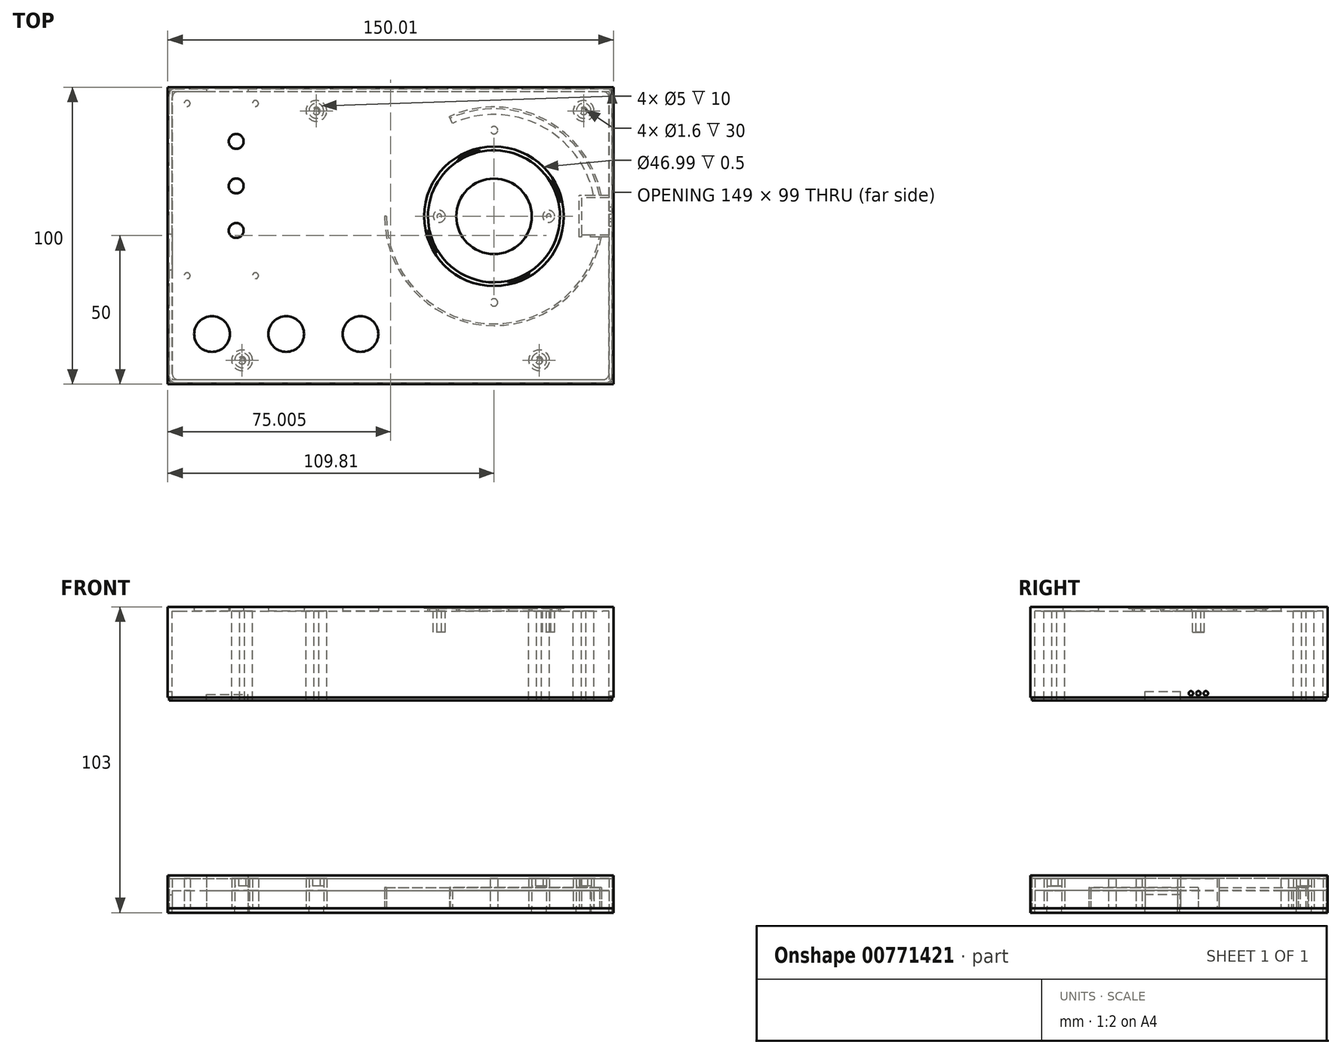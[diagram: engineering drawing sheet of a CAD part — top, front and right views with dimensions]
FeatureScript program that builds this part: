
annotation { "Feature Type Name" : "Feature", "Feature Type Description" : "" }
export const myFeature = defineFeature(function(context is Context, id is Id, definition is map)
    precondition{}
    {
        {
            var Q0;
            Q0=qCreatedBy(makeId("Top.planeOp"),FACE);
            var sketch = newSketch(context, id + "F0", { "sketchPlane" : qUnion([Q0])});
            skArc(sketch, "E0", {"start": v(-36.2, 0) * mm, "mid": v(-3.52, -36.02) * mm, "end": v(35.51, -7) * mm});
            skArc(sketch, "E1.0", {"start": v(-14.02, 31.3) * mm, "mid": v(15.6, 30.54) * mm, "end": v(33.57, 7) * mm});
            skCircle(sketch, "E2", {"center": v(0, 29) * mm, "radius": 2.5 * mm});
            skCircle(sketch, "E3", {"center": v(0, 29) * mm, "radius": 1.25 * mm});
            skCircle(sketch, "E4.1.0.0", {"center": v(0, -29) * mm, "radius": 2.5 * mm});
            skCircle(sketch, "E4.1.0.1", {"center": v(0, -29) * mm, "radius": 1.25 * mm});
            skLineSegment(sketch, "E4.direction1", {"start": v(0, 29) * mm, "end": v(0, -29) * mm, "construction": true});
            skArc(sketch, "E5", {"start": v(-36.83, 0) * mm, "mid": v(-3.52, -36.66) * mm, "end": v(36.16, -7) * mm});
            skPoint(sketch, "E6.middle", {"position": v(36.2, 0) * mm});
            skLineSegment(sketch, "E7.bottom", {"start": v(38.7, -7) * mm, "end": v(28.7, -7) * mm});
            skLineSegment(sketch, "E7.top", {"start": v(38.7, 7) * mm, "end": v(28.7, 7) * mm});
            skLineSegment(sketch, "E7.right", {"start": v(28.7, -7) * mm, "end": v(28.7, 7) * mm});
            skLineSegment(sketch, "E8", {"start": v(-34.3, 0) * mm, "end": v(-36.83, 0) * mm});
            skLineSegment(sketch, "E9", {"start": v(-14.02, 31.3) * mm, "end": v(-15.06, 33.61) * mm});
            skArc(sketch, "E10.trimOffspring", {"start": v(36.16, 7) * mm, "mid": v(16.98, 32.68) * mm, "end": v(-15.06, 33.61) * mm});
            skArc(sketch, "E11.trimOffspring", {"start": v(35.51, 7) * mm, "mid": v(16.63, 32.15) * mm, "end": v(-14.8, 33.03) * mm});
            skArc(sketch, "E12.trimOffspring", {"start": v(33.57, -7) * mm, "mid": v(-3.52, -34.1) * mm, "end": v(-34.3, 0) * mm});
            skCircle(sketch, "E13", {"center": v(-103.3, 38) * mm, "radius": 1 * mm});
            skCircle(sketch, "E14", {"center": v(-103.3, 38) * mm, "radius": 3 * mm});
            skCircle(sketch, "E15.1.0.0", {"center": v(-80.3, 38) * mm, "radius": 3 * mm});
            skCircle(sketch, "E15.1.0.1", {"center": v(-80.3, 38) * mm, "radius": 1 * mm});
            skLineSegment(sketch, "E15.direction1", {"start": v(-103.3, 38) * mm, "end": v(-80.3, 38) * mm, "construction": true});
            skLineSegment(sketch, "E16.1.0.0", {"start": v(-103.3, -20) * mm, "end": v(-80.3, -20) * mm, "construction": true});
            skCircle(sketch, "E16.1.0.1", {"center": v(-103.3, -20) * mm, "radius": 1 * mm});
            skCircle(sketch, "E16.1.0.2", {"center": v(-80.3, -20) * mm, "radius": 3 * mm});
            skCircle(sketch, "E16.1.0.3", {"center": v(-80.3, -20) * mm, "radius": 1 * mm});
            skCircle(sketch, "E16.1.0.4", {"center": v(-103.3, -20) * mm, "radius": 3 * mm});
            skLineSegment(sketch, "E16.direction1", {"start": v(-103.3, 38) * mm, "end": v(-103.3, -20) * mm, "construction": true});
            skLineSegment(sketch, "E17.bottom", {"start": v(-108.3, 42) * mm, "end": v(38.7, 42) * mm});
            skLineSegment(sketch, "E17.top", {"start": v(-108.3, -55) * mm, "end": v(38.7, -55) * mm});
            skLineSegment(sketch, "E17.left", {"start": v(-108.3, 42) * mm, "end": v(-108.3, -55) * mm});
            skLineSegment(sketch, "E17.right", {"start": v(38.7, 42) * mm, "end": v(38.7, -55) * mm});
            skLineSegment(sketch, "E18.0", {"start": v(-109.8, 43.5) * mm, "end": v(40.2, 43.5) * mm});
            skLineSegment(sketch, "E18.1", {"start": v(-109.8, 43.5) * mm, "end": v(-109.8, -56.5) * mm});
            skLineSegment(sketch, "E18.2", {"start": v(-109.8, -56.5) * mm, "end": v(40.2, -56.5) * mm});
            skLineSegment(sketch, "E18.3", {"start": v(40.2, 43.5) * mm, "end": v(40.2, -56.5) * mm});
            skLineSegment(sketch, "E19.0", {"start": v(38.7, -6.3) * mm, "end": v(29.4, -6.3) * mm});
            skLineSegment(sketch, "E19.1", {"start": v(29.4, -6.3) * mm, "end": v(29.4, 6.3) * mm});
            skLineSegment(sketch, "E19.2", {"start": v(38.7, 6.3) * mm, "end": v(29.4, 6.3) * mm});
            skLineSegment(sketch, "E20", {"start": v(38.7, 7) * mm, "end": v(38.7, 6.3) * mm});
            skLineSegment(sketch, "E21", {"start": v(38.7, -6.3) * mm, "end": v(38.7, -7) * mm});
            skLineSegment(sketch, "E22", {"start": v(29.4, -6.3) * mm, "end": v(29.4, -7) * mm});
            skLineSegment(sketch, "E23", {"start": v(32.4, -6.3) * mm, "end": v(32.4, -7) * mm});
            skLineSegment(sketch, "E24", {"start": v(-109.8, -18) * mm, "end": v(-108.3, -18) * mm});
            skLineSegment(sketch, "E25", {"start": v(-109.8, -6) * mm, "end": v(-108.3, -6) * mm});
            skLineSegment(sketch, "E26", {"start": v(-96.8, 43.5) * mm, "end": v(-96.8, 42) * mm});
            skLineSegment(sketch, "E27", {"start": v(-82.8, 43.5) * mm, "end": v(-82.8, 42) * mm});
            skCircle(sketch, "E28", {"center": v(-84.8, -48.5) * mm, "radius": 3.5 * mm});
            skCircle(sketch, "E29", {"center": v(-84.8, -48.5) * mm, "radius": 2.5 * mm});
            skCircle(sketch, "E30", {"center": v(-84.8, -48.5) * mm, "radius": 1.25 * mm});
            skCircle(sketch, "E31", {"center": v(15.2, -48.5) * mm, "radius": 3.5 * mm});
            skCircle(sketch, "E32", {"center": v(15.2, -48.5) * mm, "radius": 2.5 * mm});
            skCircle(sketch, "E33", {"center": v(15.2, -48.5) * mm, "radius": 1.25 * mm});
            skCircle(sketch, "E34", {"center": v(-59.8, 35.5) * mm, "radius": 3.5 * mm});
            skCircle(sketch, "E35", {"center": v(-59.8, 35.5) * mm, "radius": 2.5 * mm});
            skCircle(sketch, "E36", {"center": v(-59.8, 35.5) * mm, "radius": 1.25 * mm});
            skCircle(sketch, "E37", {"center": v(30.2, 35.5) * mm, "radius": 3.5 * mm});
            skCircle(sketch, "E38", {"center": v(30.2, 35.5) * mm, "radius": 2.5 * mm});
            skCircle(sketch, "E39", {"center": v(30.2, 35.5) * mm, "radius": 1.25 * mm});
            skLineSegment(sketch, "E40.0", {"start": v(-109.3, -56) * mm, "end": v(39.7, -56) * mm});
            skLineSegment(sketch, "E40.1", {"start": v(-109.3, 43) * mm, "end": v(-109.3, -6) * mm});
            skLineSegment(sketch, "E40.2", {"start": v(-109.3, 43) * mm, "end": v(-96.8, 43) * mm});
            skLineSegment(sketch, "E40.3", {"start": v(39.7, 43) * mm, "end": v(39.7, -56) * mm});
            skLineSegment(sketch, "E41.trimOffspring", {"start": v(-109.3, -18) * mm, "end": v(-109.3, -56) * mm});
            skLineSegment(sketch, "E42.trimOffspring", {"start": v(-82.8, 43) * mm, "end": v(39.7, 43) * mm});
            skSolve(sketch);
        }
        {
            var Q0;
            {var subQ0=sQuery(id+"F0.wireOp",EDGE,"E1.0");Q0=makeQuery(id+"F0.imprint","IMPRINT",FACE,{"disambiguationData":[TD([[makeQuery(id+"F0.imprint","IMPRINT",EDGE,{"derivedFrom":subQ0}),1.0]])]});}
            var Q1;
            {var subQ0=sQuery(id+"F0.wireOp",EDGE,"E0");Q1=makeQuery(id+"F0.imprint","IMPRINT",FACE,{"disambiguationData":[TD([[makeQuery(id+"F0.imprint","IMPRINT",EDGE,{"derivedFrom":subQ0}),1.0]])]});}
            var Q2;
            Q2=makeQuery(id+"F0.imprint","IMPRINT",FACE,{"disambiguationData":[TD([[makeQuery(id+"F0.imprint","IMPRINT",EDGE,{"derivedFrom":sQuery(id+"F0.wireOp",EDGE,"E4.1.0.0")}),1.0]])]});
            var Q3;
            Q3=makeQuery(id+"F0.imprint","IMPRINT",FACE,{"disambiguationData":[TD([[makeQuery(id+"F0.imprint","IMPRINT",EDGE,{"derivedFrom":sQuery(id+"F0.wireOp",EDGE,"E2")}),1.0]])]});
            var Q4;
            Q4=makeQuery(id+"F0.imprint","IMPRINT",FACE,{"disambiguationData":[TD([[makeQuery(id+"F0.imprint","IMPRINT",EDGE,{"derivedFrom":sQuery(id+"F0.wireOp",EDGE,"E15.1.0.0")}),1.0]])]});
            var Q5;
            Q5=makeQuery(id+"F0.imprint","IMPRINT",FACE,{"disambiguationData":[TD([[makeQuery(id+"F0.imprint","IMPRINT",EDGE,{"derivedFrom":sQuery(id+"F0.wireOp",EDGE,"E13")}),-1.0]])]});
            var Q6;
            Q6=makeQuery(id+"F0.imprint","IMPRINT",FACE,{"disambiguationData":[TD([[makeQuery(id+"F0.imprint","IMPRINT",EDGE,{"derivedFrom":sQuery(id+"F0.wireOp",EDGE,"E16.1.0.2")}),1.0]])]});
            var Q7;
            Q7=makeQuery(id+"F0.imprint","IMPRINT",FACE,{"disambiguationData":[TD([[makeQuery(id+"F0.imprint","IMPRINT",EDGE,{"derivedFrom":sQuery(id+"F0.wireOp",EDGE,"E16.1.0.1")}),-1.0]])]});
            var Q8;
            {var subQ0=sQuery(id+"F0.wireOp",EDGE,"E22");Q8=makeQuery(id+"F0.imprint","IMPRINT",FACE,{"disambiguationData":[TD([[makeQuery(id+"F0.imprint","IMPRINT",EDGE,{"derivedFrom":subQ0}),1.0]])]});}
            var Q9;
            {var subQ0=sQuery(id+"F0.wireOp",EDGE,"E26");Q9=makeQuery(id+"F0.imprint","IMPRINT",FACE,{"disambiguationData":[TD([[makeQuery(id+"F0.imprint","IMPRINT",EDGE,{"derivedFrom":subQ0}),1.0]])]});}
            extrude(context, id + "F1", {"entities" : qUnion([Q0, Q1, Q2, Q3, Q4, Q5, Q6, Q7, Q8, Q9]), "depth" : 6 * mm, "offsetDistance" : 25 * mm});
        }
        {
            var Q0;
            Q0=makeQuery(id+"F0.imprint","IMPRINT",FACE,{"disambiguationData":[TD([[makeQuery(id+"F0.imprint","IMPRINT",EDGE,{"derivedFrom":sQuery(id+"F0.wireOp",EDGE,"E3")}),1.0]])]});
            var Q1;
            Q1=makeQuery(id+"F0.imprint","IMPRINT",FACE,{"disambiguationData":[TD([[makeQuery(id+"F0.imprint","IMPRINT",EDGE,{"derivedFrom":sQuery(id+"F0.wireOp",EDGE,"E4.1.0.1")}),1.0]])]});
            var Q2;
            Q2=makeQuery(id+"F0.imprint","IMPRINT",FACE,{"disambiguationData":[TD([[makeQuery(id+"F0.imprint","IMPRINT",EDGE,{"derivedFrom":sQuery(id+"F0.wireOp",EDGE,"E13")}),1.0]])]});
            var Q3;
            Q3=makeQuery(id+"F0.imprint","IMPRINT",FACE,{"disambiguationData":[TD([[makeQuery(id+"F0.imprint","IMPRINT",EDGE,{"derivedFrom":sQuery(id+"F0.wireOp",EDGE,"E15.1.0.1")}),1.0]])]});
            var Q4;
            Q4=makeQuery(id+"F0.imprint","IMPRINT",FACE,{"disambiguationData":[TD([[makeQuery(id+"F0.imprint","IMPRINT",EDGE,{"derivedFrom":sQuery(id+"F0.wireOp",EDGE,"E16.1.0.3")}),1.0]])]});
            var Q5;
            Q5=makeQuery(id+"F0.imprint","IMPRINT",FACE,{"disambiguationData":[TD([[makeQuery(id+"F0.imprint","IMPRINT",EDGE,{"derivedFrom":sQuery(id+"F0.wireOp",EDGE,"E16.1.0.1")}),1.0]])]});
            extrude(context, id + "F2", {"entities" : qUnion([Q0, Q1, Q2, Q3, Q4, Q5]), "depth" : 10 * mm, "offsetDistance" : 25 * mm});
        }
        {
            var Q0;
            {var subQ0=sQuery(id+"F0.wireOp",EDGE,"E7.right");Q0=makeQuery(id+"F0.imprint","IMPRINT",FACE,{"disambiguationData":[TD([[makeQuery(id+"F0.imprint","IMPRINT",EDGE,{"derivedFrom":subQ0}),-1.0]])]});}
            var Q1;
            {var subQ4=sQuery(id+"F0.wireOp",EDGE,"E21");Q1=makeQuery(id+"F0.imprint","IMPRINT",FACE,{"disambiguationData":[TD([[makeQuery(id+"F0.imprint","IMPRINT",EDGE,{"derivedFrom":subQ4}),-1.0]])]});}
            var Q2;
            Q2=makeQuery(id+"F0.imprint","IMPRINT",FACE,{"disambiguationData":[TD([[makeQuery(id+"F0.imprint","IMPRINT",EDGE,{"derivedFrom":sQuery(id+"F0.wireOp",EDGE,"E31")}),1.0]])]});
            var Q3;
            Q3=makeQuery(id+"F0.imprint","IMPRINT",FACE,{"disambiguationData":[TD([[makeQuery(id+"F0.imprint","IMPRINT",EDGE,{"derivedFrom":sQuery(id+"F0.wireOp",EDGE,"E37")}),1.0]])]});
            var Q4;
            Q4=makeQuery(id+"F0.imprint","IMPRINT",FACE,{"disambiguationData":[TD([[makeQuery(id+"F0.imprint","IMPRINT",EDGE,{"derivedFrom":sQuery(id+"F0.wireOp",EDGE,"E28")}),1.0]])]});
            var Q5;
            Q5=makeQuery(id+"F0.imprint","IMPRINT",FACE,{"disambiguationData":[TD([[makeQuery(id+"F0.imprint","IMPRINT",EDGE,{"derivedFrom":sQuery(id+"F0.wireOp",EDGE,"E34")}),1.0]])]});
            extrude(context, id + "F3", {"entities" : qUnion([Q0, Q1, Q2, Q3, Q4, Q5]), "depth" : 10 * mm, "offsetDistance" : 25 * mm});
        }
        {
            var Q0;
            {var subQ3=sQuery(id+"F0.wireOp",EDGE,"8f94c075-a68a-4a81-960c-e8ac357c0ef5.0");Q0=makeQuery(id+"F0.imprint","IMPRINT",FACE,{"disambiguationData":[TD([[makeQuery(id+"F0.imprint","IMPRINT",EDGE,{"derivedFrom":subQ3}),-1.0]])]});}
            var Q1;
            {var subQ11=sQuery(id+"F0.wireOp",EDGE,"E17.top");Q1=makeQuery(id+"F0.imprint","IMPRINT",FACE,{"disambiguationData":[TD([[makeQuery(id+"F0.imprint","IMPRINT",EDGE,{"derivedFrom":subQ11}),-1.0]])]});}
            var Q2;
            {var subQ3=sQuery(id+"F0.wireOp",EDGE,"E40.1");Q2=makeQuery(id+"F0.imprint","IMPRINT",FACE,{"disambiguationData":[TD([[makeQuery(id+"F0.imprint","IMPRINT",EDGE,{"derivedFrom":subQ3}),1.0]])]});}
            extrude(context, id + "F4", {"entities" : qUnion([Q0, Q1, Q2]), "depth" : 10 * mm, "offsetDistance" : 25 * mm});
        }
        {
            var Q0;
            {var subQ0=sQuery(id+"F0.wireOp",EDGE,"E24");Q0=makeQuery(id+"F0.imprint","IMPRINT",FACE,{"disambiguationData":[TD([[makeQuery(id+"F0.imprint","IMPRINT",EDGE,{"derivedFrom":subQ0}),1.0]])]});}
            extrude(context, id + "F5", {"entities" : qUnion([Q0]), "depth" : 4.5 * mm, "offsetDistance" : 25 * mm});
        }
        {
            var Q0;
            {var subQ8=sQuery(id+"F0.wireOp",EDGE,"8f94c075-a68a-4a81-960c-e8ac357c0ef5.0");Q0=makeQuery(id+"F0.imprint","IMPRINT",FACE,{"disambiguationData":[TD([[makeQuery(id+"F0.imprint","IMPRINT",EDGE,{"derivedFrom":subQ8}),1.0]])]});}
            var Q1;
            {var subQ0=sQuery(id+"F0.wireOp",EDGE,"E18.2");Q1=makeQuery(id+"F0.imprint","IMPRINT",FACE,{"disambiguationData":[TD([[makeQuery(id+"F0.imprint","IMPRINT",EDGE,{"derivedFrom":subQ0}),1.0]])]});}
            var Q2;
            {var subQ3=sQuery(id+"F0.wireOp",EDGE,"E40.1");Q2=makeQuery(id+"F0.imprint","IMPRINT",FACE,{"disambiguationData":[TD([[makeQuery(id+"F0.imprint","IMPRINT",EDGE,{"derivedFrom":subQ3}),-1.0]])]});}
            extrude(context, id + "F6", {"entities" : qUnion([Q0, Q1, Q2]), "depth" : 11 * mm, "offsetDistance" : 25 * mm});
        }
        {
            var Q0;
            {var subQ0=sQuery(id+"F0.wireOp",EDGE,"E10.trimOffspring");Q0=makeQuery(id+"F0.imprint","IMPRINT",FACE,{"disambiguationData":[TD([[makeQuery(id+"F0.imprint","IMPRINT",EDGE,{"derivedFrom":subQ0}),1.0]])]});}
            var Q1;
            {var subQ0=sQuery(id+"F0.wireOp",EDGE,"E0");Q1=makeQuery(id+"F0.imprint","IMPRINT",FACE,{"disambiguationData":[TD([[makeQuery(id+"F0.imprint","IMPRINT",EDGE,{"derivedFrom":subQ0}),-1.0]])]});}
            extrude(context, id + "F7", {"entities" : qUnion([Q0, Q1]), "depth" : 7 * mm, "offsetDistance" : 25 * mm});
        }
        {
            var Q0;
            Q0=makeQuery(id+"F0.imprint","IMPRINT",FACE,{"disambiguationData":[TD([[makeQuery(id+"F0.imprint","IMPRINT",EDGE,{"derivedFrom":sQuery(id+"F0.wireOp",EDGE,"E29")}),1.0]])]});
            var Q1;
            Q1=makeQuery(id+"F0.imprint","IMPRINT",FACE,{"disambiguationData":[TD([[makeQuery(id+"F0.imprint","IMPRINT",EDGE,{"derivedFrom":sQuery(id+"F0.wireOp",EDGE,"E35")}),1.0]])]});
            var Q2;
            Q2=makeQuery(id+"F0.imprint","IMPRINT",FACE,{"disambiguationData":[TD([[makeQuery(id+"F0.imprint","IMPRINT",EDGE,{"derivedFrom":sQuery(id+"F0.wireOp",EDGE,"E32")}),1.0]])]});
            var Q3;
            Q3=makeQuery(id+"F0.imprint","IMPRINT",FACE,{"disambiguationData":[TD([[makeQuery(id+"F0.imprint","IMPRINT",EDGE,{"derivedFrom":sQuery(id+"F0.wireOp",EDGE,"E38")}),1.0]])]});
            extrude(context, id + "F8", {"entities" : qUnion([Q0, Q1, Q2, Q3]), "depth" : 10 * mm, "offsetDistance" : 25 * mm, "hasSecondDirection" : true, "secondDirectionOppositeDirection" : true, "secondDirectionDepth" : -7.5 * mm});
        }
        {
            var Q0;
            {var subQ0=sQuery(id+"F0.wireOp",EDGE,"E18.2");Q0=makeQuery(id+"F0.imprint","IMPRINT",FACE,{"disambiguationData":[TD([[makeQuery(id+"F0.imprint","IMPRINT",EDGE,{"derivedFrom":subQ0}),1.0]])]});}
            var Q1;
            {var subQ2=sQuery(id+"F0.wireOp",EDGE,"E20");Q1=makeQuery(id+"F0.imprint","IMPRINT",FACE,{"disambiguationData":[TD([[makeQuery(id+"F0.imprint","IMPRINT",EDGE,{"derivedFrom":subQ2}),1.0]])]});}
            var Q2;
            {var subQ0=sQuery(id+"F0.wireOp",EDGE,"E24");var subQ1=sQuery(id+"F0.wireOp",EDGE,"E17.left");var subQ2=makeQuery(id+"F0.imprint","INTERSECT",VERTEX,{"derivedFrom":[subQ1,subQ0]});Q2=makeQuery(id+"F0.imprint","IMPRINT",FACE,{"disambiguationData":[TD([[makeQuery(id+"F0.imprint","IMPRINT",EDGE,{"disambiguationData":[TD([[subQ2,1.0]])],"derivedFrom":subQ1}),-1.0]])]});}
            var Q3;
            {var subQ3=sQuery(id+"F0.wireOp",EDGE,"E40.1");Q3=makeQuery(id+"F0.imprint","IMPRINT",FACE,{"disambiguationData":[TD([[makeQuery(id+"F0.imprint","IMPRINT",EDGE,{"derivedFrom":subQ3}),-1.0]])]});}
            var Q4;
            {var subQ3=sQuery(id+"F0.wireOp",EDGE,"E40.1");Q4=makeQuery(id+"F0.imprint","IMPRINT",FACE,{"disambiguationData":[TD([[makeQuery(id+"F0.imprint","IMPRINT",EDGE,{"derivedFrom":subQ3}),1.0]])]});}
            var Q5;
            {var subQ0=sQuery(id+"F0.wireOp",EDGE,"E26");var subQ4=sQuery(id+"F0.wireOp",EDGE,"E17.bottom");var subQ5=makeQuery(id+"F0.imprint","INTERSECT",VERTEX,{"derivedFrom":[subQ4,subQ0]});Q5=makeQuery(id+"F0.imprint","IMPRINT",FACE,{"disambiguationData":[TD([[makeQuery(id+"F0.imprint","IMPRINT",EDGE,{"disambiguationData":[TD([[subQ5,-1.0]])],"derivedFrom":subQ4}),1.0]])]});}
            var Q6;
            {var subQ8=sQuery(id+"F0.wireOp",EDGE,"E1.0");Q6=makeQuery(id+"F0.imprint","IMPRINT",FACE,{"disambiguationData":[TD([[makeQuery(id+"F0.imprint","IMPRINT",EDGE,{"derivedFrom":subQ8}),-1.0]])]});}
            var Q7;
            Q7=makeQuery(id+"F0.imprint","IMPRINT",FACE,{"disambiguationData":[TD([[makeQuery(id+"F0.imprint","IMPRINT",EDGE,{"derivedFrom":sQuery(id+"F0.wireOp",EDGE,"E13")}),-1.0]])]});
            var Q8;
            Q8=makeQuery(id+"F0.imprint","IMPRINT",FACE,{"disambiguationData":[TD([[makeQuery(id+"F0.imprint","IMPRINT",EDGE,{"derivedFrom":sQuery(id+"F0.wireOp",EDGE,"E13")}),1.0]])]});
            var Q9;
            Q9=makeQuery(id+"F0.imprint","IMPRINT",FACE,{"disambiguationData":[TD([[makeQuery(id+"F0.imprint","IMPRINT",EDGE,{"derivedFrom":sQuery(id+"F0.wireOp",EDGE,"E15.1.0.0")}),1.0]])]});
            var Q10;
            Q10=makeQuery(id+"F0.imprint","IMPRINT",FACE,{"disambiguationData":[TD([[makeQuery(id+"F0.imprint","IMPRINT",EDGE,{"derivedFrom":sQuery(id+"F0.wireOp",EDGE,"E15.1.0.1")}),1.0]])]});
            var Q11;
            Q11=makeQuery(id+"F0.imprint","IMPRINT",FACE,{"disambiguationData":[TD([[makeQuery(id+"F0.imprint","IMPRINT",EDGE,{"derivedFrom":sQuery(id+"F0.wireOp",EDGE,"E34")}),1.0]])]});
            var Q12;
            Q12=makeQuery(id+"F0.imprint","IMPRINT",FACE,{"disambiguationData":[TD([[makeQuery(id+"F0.imprint","IMPRINT",EDGE,{"derivedFrom":sQuery(id+"F0.wireOp",EDGE,"E28")}),1.0]])]});
            var Q13;
            Q13=makeQuery(id+"F0.imprint","IMPRINT",FACE,{"disambiguationData":[TD([[makeQuery(id+"F0.imprint","IMPRINT",EDGE,{"derivedFrom":sQuery(id+"F0.wireOp",EDGE,"E16.1.0.1")}),-1.0]])]});
            var Q14;
            Q14=makeQuery(id+"F0.imprint","IMPRINT",FACE,{"disambiguationData":[TD([[makeQuery(id+"F0.imprint","IMPRINT",EDGE,{"derivedFrom":sQuery(id+"F0.wireOp",EDGE,"E16.1.0.1")}),1.0]])]});
            var Q15;
            Q15=makeQuery(id+"F0.imprint","IMPRINT",FACE,{"disambiguationData":[TD([[makeQuery(id+"F0.imprint","IMPRINT",EDGE,{"derivedFrom":sQuery(id+"F0.wireOp",EDGE,"E16.1.0.2")}),1.0]])]});
            var Q16;
            Q16=makeQuery(id+"F0.imprint","IMPRINT",FACE,{"disambiguationData":[TD([[makeQuery(id+"F0.imprint","IMPRINT",EDGE,{"derivedFrom":sQuery(id+"F0.wireOp",EDGE,"E16.1.0.3")}),1.0]])]});
            var Q17;
            Q17=makeQuery(id+"F0.imprint","IMPRINT",FACE,{"disambiguationData":[TD([[makeQuery(id+"F0.imprint","IMPRINT",EDGE,{"derivedFrom":sQuery(id+"F0.wireOp",EDGE,"E2")}),1.0]])]});
            var Q18;
            Q18=makeQuery(id+"F0.imprint","IMPRINT",FACE,{"disambiguationData":[TD([[makeQuery(id+"F0.imprint","IMPRINT",EDGE,{"derivedFrom":sQuery(id+"F0.wireOp",EDGE,"E3")}),1.0]])]});
            var Q19;
            {var subQ0=sQuery(id+"F0.wireOp",EDGE,"E1.0");Q19=makeQuery(id+"F0.imprint","IMPRINT",FACE,{"disambiguationData":[TD([[makeQuery(id+"F0.imprint","IMPRINT",EDGE,{"derivedFrom":subQ0}),1.0]])]});}
            var Q20;
            {var subQ0=sQuery(id+"F0.wireOp",EDGE,"E10.trimOffspring");Q20=makeQuery(id+"F0.imprint","IMPRINT",FACE,{"disambiguationData":[TD([[makeQuery(id+"F0.imprint","IMPRINT",EDGE,{"derivedFrom":subQ0}),1.0]])]});}
            var Q21;
            {var subQ1=sQuery(id+"F0.wireOp",EDGE,"E0");Q21=makeQuery(id+"F0.imprint","IMPRINT",FACE,{"disambiguationData":[TD([[makeQuery(id+"F0.imprint","IMPRINT",EDGE,{"derivedFrom":subQ1}),1.0]])]});}
            var Q22;
            {var subQ0=sQuery(id+"F0.wireOp",EDGE,"E0");Q22=makeQuery(id+"F0.imprint","IMPRINT",FACE,{"disambiguationData":[TD([[makeQuery(id+"F0.imprint","IMPRINT",EDGE,{"derivedFrom":subQ0}),-1.0]])]});}
            var Q23;
            Q23=makeQuery(id+"F0.imprint","IMPRINT",FACE,{"disambiguationData":[TD([[makeQuery(id+"F0.imprint","IMPRINT",EDGE,{"derivedFrom":sQuery(id+"F0.wireOp",EDGE,"E37")}),1.0]])]});
            var Q24;
            {var subQ5=sQuery(id+"F0.wireOp",EDGE,"E7.right");Q24=makeQuery(id+"F0.imprint","IMPRINT",FACE,{"disambiguationData":[TD([[makeQuery(id+"F0.imprint","IMPRINT",EDGE,{"derivedFrom":subQ5}),-1.0]])]});}
            var Q25;
            {var subQ0=sQuery(id+"F0.wireOp",EDGE,"E19.1");Q25=makeQuery(id+"F0.imprint","IMPRINT",FACE,{"disambiguationData":[TD([[makeQuery(id+"F0.imprint","IMPRINT",EDGE,{"derivedFrom":subQ0}),-1.0]])]});}
            var Q26;
            {var subQ0=sQuery(id+"F0.wireOp",EDGE,"E21");Q26=makeQuery(id+"F0.imprint","IMPRINT",FACE,{"disambiguationData":[TD([[makeQuery(id+"F0.imprint","IMPRINT",EDGE,{"derivedFrom":subQ0}),-1.0]])]});}
            var Q27;
            {var subQ0=sQuery(id+"F0.wireOp",EDGE,"E22");Q27=makeQuery(id+"F0.imprint","IMPRINT",FACE,{"disambiguationData":[TD([[makeQuery(id+"F0.imprint","IMPRINT",EDGE,{"derivedFrom":subQ0}),1.0]])]});}
            var Q28;
            Q28=makeQuery(id+"F0.imprint","IMPRINT",FACE,{"disambiguationData":[TD([[makeQuery(id+"F0.imprint","IMPRINT",EDGE,{"derivedFrom":sQuery(id+"F0.wireOp",EDGE,"E4.1.0.0")}),1.0]])]});
            var Q29;
            Q29=makeQuery(id+"F0.imprint","IMPRINT",FACE,{"disambiguationData":[TD([[makeQuery(id+"F0.imprint","IMPRINT",EDGE,{"derivedFrom":sQuery(id+"F0.wireOp",EDGE,"E4.1.0.1")}),1.0]])]});
            var Q30;
            Q30=makeQuery(id+"F0.imprint","IMPRINT",FACE,{"disambiguationData":[TD([[makeQuery(id+"F0.imprint","IMPRINT",EDGE,{"derivedFrom":sQuery(id+"F0.wireOp",EDGE,"E31")}),1.0]])]});
            extrude(context, id + "F9", {"entities" : qUnion([Q0, Q1, Q2, Q3, Q4, Q5, Q6, Q7, Q8, Q9, Q10, Q11, Q12, Q13, Q14, Q15, Q16, Q17, Q18, Q19, Q20, Q21, Q22, Q23, Q24, Q25, Q26, Q27, Q28, Q29, Q30]), "oppositeDirection" : true, "depth" : 1.5 * mm, "offsetDistance" : 25 * mm});
        }
        {
            var Q0;
            Q0=makeQuery(id+"F4.opExtrude","SWEPT_EDGE",EDGE,{"disambiguationData":[OSD([sQuery(id+"F0.wireOp",EDGE,"E17.bottom"),sQuery(id+"F0.wireOp",EDGE,"E17.right")])]});
            var Q1;
            Q1=makeQuery(id+"F6.opExtrude","SWEPT_EDGE",EDGE,{"disambiguationData":[OSD([sQuery(id+"F0.wireOp",EDGE,"E40.3"),sQuery(id+"F0.wireOp",EDGE,"E42.trimOffspring")])]});
            var Q2;
            Q2=makeQuery(id+"F9.opExtrude","SWEPT_EDGE",EDGE,{"disambiguationData":[OSD([sQuery(id+"F0.wireOp",EDGE,"E18.0"),sQuery(id+"F0.wireOp",EDGE,"E18.3")])]});
            var Q3;
            Q3=makeQuery(id+"F6.opExtrude","SWEPT_EDGE",EDGE,{"disambiguationData":[OSD([sQuery(id+"F0.wireOp",EDGE,"E18.0"),sQuery(id+"F0.wireOp",EDGE,"E18.3")])]});
            var Q4;
            Q4=makeQuery(id+"F9.opExtrude","SWEPT_EDGE",EDGE,{"disambiguationData":[OSD([sQuery(id+"F0.wireOp",EDGE,"E18.2"),sQuery(id+"F0.wireOp",EDGE,"E18.3")])]});
            var Q5;
            Q5=makeQuery(id+"F6.opExtrude","SWEPT_EDGE",EDGE,{"disambiguationData":[OSD([sQuery(id+"F0.wireOp",EDGE,"E18.2"),sQuery(id+"F0.wireOp",EDGE,"E18.3")])]});
            var Q6;
            Q6=makeQuery(id+"F4.opExtrude","SWEPT_EDGE",EDGE,{"disambiguationData":[OSD([sQuery(id+"F0.wireOp",EDGE,"E17.top"),sQuery(id+"F0.wireOp",EDGE,"E17.right")])]});
            var Q7;
            Q7=makeQuery(id+"F6.opExtrude","SWEPT_EDGE",EDGE,{"disambiguationData":[OSD([sQuery(id+"F0.wireOp",EDGE,"E40.0"),sQuery(id+"F0.wireOp",EDGE,"E40.3")])]});
            var Q8;
            Q8=makeQuery(id+"F4.opExtrude","SWEPT_EDGE",EDGE,{"disambiguationData":[OSD([sQuery(id+"F0.wireOp",EDGE,"E17.bottom"),sQuery(id+"F0.wireOp",EDGE,"E17.left")])]});
            var Q9;
            Q9=makeQuery(id+"F6.opExtrude","SWEPT_EDGE",EDGE,{"disambiguationData":[OSD([sQuery(id+"F0.wireOp",EDGE,"E40.1"),sQuery(id+"F0.wireOp",EDGE,"E40.2")])]});
            var Q10;
            Q10=makeQuery(id+"F4.opExtrude","SWEPT_EDGE",EDGE,{"disambiguationData":[OSD([sQuery(id+"F0.wireOp",EDGE,"E17.top"),sQuery(id+"F0.wireOp",EDGE,"E17.left")])]});
            var Q11;
            Q11=makeQuery(id+"F6.opExtrude","SWEPT_EDGE",EDGE,{"disambiguationData":[OSD([sQuery(id+"F0.wireOp",EDGE,"E40.0"),sQuery(id+"F0.wireOp",EDGE,"E41.trimOffspring")])]});
            var Q12;
            Q12=makeQuery(id+"F9.opExtrude","SWEPT_EDGE",EDGE,{"disambiguationData":[OSD([sQuery(id+"F0.wireOp",EDGE,"E18.0"),sQuery(id+"F0.wireOp",EDGE,"E18.1")])]});
            var Q13;
            Q13=makeQuery(id+"F6.opExtrude","SWEPT_EDGE",EDGE,{"disambiguationData":[OSD([sQuery(id+"F0.wireOp",EDGE,"E18.0"),sQuery(id+"F0.wireOp",EDGE,"E18.1")])]});
            var Q14;
            Q14=makeQuery(id+"F9.opExtrude","SWEPT_EDGE",EDGE,{"disambiguationData":[OSD([sQuery(id+"F0.wireOp",EDGE,"E18.1"),sQuery(id+"F0.wireOp",EDGE,"E18.2")])]});
            var Q15;
            Q15=makeQuery(id+"F6.opExtrude","SWEPT_EDGE",EDGE,{"disambiguationData":[OSD([sQuery(id+"F0.wireOp",EDGE,"E18.1"),sQuery(id+"F0.wireOp",EDGE,"E18.2")])]});
            fillet(context, id + "F10", {"entities" : qUnion([Q0, Q1, Q2, Q3, Q4, Q5, Q6, Q7, Q8, Q9, Q10, Q11, Q12, Q13, Q14, Q15]), "radius" : 2 * mm, "tangentPropagation" : true, "allowEdgeOverflow" : false});
        }
        {
            var Q0;
            Q0=makeQuery(id+"F4.opExtrude","SWEPT_EDGE",EDGE,{"disambiguationData":[OSD([sQuery(id+"F0.wireOp",EDGE,"E40.0"),sQuery(id+"F0.wireOp",EDGE,"E40.3")])]});
            var Q1;
            Q1=makeQuery(id+"F4.opExtrude","SWEPT_EDGE",EDGE,{"disambiguationData":[OSD([sQuery(id+"F0.wireOp",EDGE,"E40.3"),sQuery(id+"F0.wireOp",EDGE,"E42.trimOffspring")])]});
            var Q2;
            Q2=makeQuery(id+"F4.opExtrude","SWEPT_EDGE",EDGE,{"disambiguationData":[OSD([sQuery(id+"F0.wireOp",EDGE,"E40.1"),sQuery(id+"F0.wireOp",EDGE,"E40.2")])]});
            var Q3;
            Q3=makeQuery(id+"F4.opExtrude","SWEPT_EDGE",EDGE,{"disambiguationData":[OSD([sQuery(id+"F0.wireOp",EDGE,"E40.0"),sQuery(id+"F0.wireOp",EDGE,"E41.trimOffspring")])]});
            fillet(context, id + "F11", {"entities" : qUnion([Q0, Q1, Q2, Q3]), "radius" : 2 * mm, "tangentPropagation" : true, "allowEdgeOverflow" : false});
        }
        {
            var Q0;
            Q0=qCreatedBy(makeId("Top.planeOp"),FACE);
            cPlane(context, id + "F12", {"entities" : qUnion([Q0]), "cplaneType" : CPlaneType.OFFSET, "offset" : 100 * mm, "width" : 150 * mm, "height" : 150 * mm});
        }
        {
            var Q0;
            Q0=qCreatedBy(id+"F12.planeOp",FACE);
            var sketch = newSketch(context, id + "F13", { "sketchPlane" : qUnion([Q0])});
            skLineSegment(sketch, "E43.bottom", {"start": v(-109.8, -56.5) * mm, "end": v(40.2, -56.5) * mm});
            skLineSegment(sketch, "E43.top", {"start": v(-109.8, 43.5) * mm, "end": v(40.2, 43.5) * mm});
            skLineSegment(sketch, "E43.left", {"start": v(-109.8, -56.5) * mm, "end": v(-109.8, 43.5) * mm});
            skLineSegment(sketch, "E43.right", {"start": v(40.2, -56.5) * mm, "end": v(40.2, 43.5) * mm});
            skCircle(sketch, "E44", {"center": v(-84.8, -48.5) * mm, "radius": 3.5 * mm});
            skCircle(sketch, "E45", {"center": v(15.2, -48.5) * mm, "radius": 3.5 * mm});
            skCircle(sketch, "E46", {"center": v(30.2, 35.5) * mm, "radius": 3.5 * mm});
            skCircle(sketch, "E47", {"center": v(-59.8, 35.5) * mm, "radius": 3.5 * mm});
            skCircle(sketch, "E48", {"center": v(-94.94, -39.66) * mm, "radius": 6 * mm});
            skCircle(sketch, "E49.1.0.0", {"center": v(-69.94, -39.66) * mm, "radius": 6 * mm});
            skCircle(sketch, "E49.2.0.0", {"center": v(-44.94, -39.66) * mm, "radius": 6 * mm});
            skLineSegment(sketch, "E49.direction1", {"start": v(-94.94, -39.66) * mm, "end": v(-69.94, -39.66) * mm, "construction": true});
            skCircle(sketch, "E50", {"center": v(-86.8, -4.78) * mm, "radius": 2.5 * mm});
            skCircle(sketch, "E51.1.0.0", {"center": v(-86.8, 10.22) * mm, "radius": 2.5 * mm});
            skCircle(sketch, "E51.2.0.0", {"center": v(-86.8, 25.22) * mm, "radius": 2.5 * mm});
            skLineSegment(sketch, "E51.direction1", {"start": v(-86.8, -4.78) * mm, "end": v(-86.8, 10.22) * mm, "construction": true});
            skPoint(sketch, "E52.middle", {"position": v(0, 0) * mm});
            skCircle(sketch, "E53", {"center": v(-18.41, 0) * mm, "radius": 2 * mm});
            skCircle(sketch, "E54.1.0.0", {"center": v(18.42, 0) * mm, "radius": 2 * mm});
            skLineSegment(sketch, "E54.direction1", {"start": v(-18.42, 0) * mm, "end": v(18.42, 0) * mm, "construction": true});
            skCircle(sketch, "E55", {"center": v(0, 0) * mm, "radius": 12.7 * mm});
            skCircle(sketch, "E56", {"center": v(0, 0) * mm, "radius": 22.23 * mm});
            skCircle(sketch, "E57", {"center": v(0, 0) * mm, "radius": 23.5 * mm});
            skLineSegment(sketch, "E58", {"start": v(-22.32, -4.95) * mm, "end": v(-21.7, -4.81) * mm});
            skLineSegment(sketch, "E59", {"start": v(-12.07, 19.42) * mm, "end": v(-11.73, 18.88) * mm});
            skLineSegment(sketch, "E60", {"start": v(-4.95, 22.32) * mm, "end": v(-4.81, 21.7) * mm});
            skLineSegment(sketch, "E61", {"start": v(19.42, 12.07) * mm, "end": v(18.88, 11.73) * mm});
            skLineSegment(sketch, "E62.trimOffspring", {"start": v(21.7, 4.81) * mm, "end": v(22.32, 4.95) * mm});
            skLineSegment(sketch, "E63.trimOffspring", {"start": v(11.73, -18.88) * mm, "end": v(12.07, -19.42) * mm});
            skLineSegment(sketch, "E64.trimOffspring", {"start": v(4.81, -21.7) * mm, "end": v(4.95, -22.32) * mm});
            skLineSegment(sketch, "E65.trimOffspring", {"start": v(-18.88, -11.73) * mm, "end": v(-19.42, -12.07) * mm});
            skLineSegment(sketch, "E66.0", {"start": v(-109.3, 43) * mm, "end": v(-96.8, 43) * mm});
            skLineSegment(sketch, "E66.1", {"start": v(-109.3, -56) * mm, "end": v(-109.3, -18) * mm});
            skLineSegment(sketch, "E66.2", {"start": v(-109.3, -56) * mm, "end": v(39.7, -56) * mm});
            skLineSegment(sketch, "E66.3", {"start": v(39.7, -56) * mm, "end": v(39.7, 43) * mm});
            skLineSegment(sketch, "E67.0", {"start": v(-108.3, 42) * mm, "end": v(38.7, 42) * mm});
            skLineSegment(sketch, "E67.1", {"start": v(-108.3, -55) * mm, "end": v(-108.3, 42) * mm});
            skLineSegment(sketch, "E67.2", {"start": v(-108.3, -55) * mm, "end": v(38.7, -55) * mm});
            skLineSegment(sketch, "E67.3", {"start": v(38.7, -55) * mm, "end": v(38.7, 42) * mm});
            skLineSegment(sketch, "E68", {"start": v(-109.8, -18) * mm, "end": v(-108.3, -18) * mm});
            skLineSegment(sketch, "E69", {"start": v(-109.8, -6) * mm, "end": v(-108.3, -6) * mm});
            skLineSegment(sketch, "E70", {"start": v(-96.8, 43.5) * mm, "end": v(-96.8, 42) * mm});
            skLineSegment(sketch, "E71", {"start": v(-82.8, 43.5) * mm, "end": v(-82.8, 42) * mm});
            skLineSegment(sketch, "E72.trimOffspring", {"start": v(-82.8, 43) * mm, "end": v(39.7, 43) * mm});
            skLineSegment(sketch, "E73.trimOffspring", {"start": v(-109.3, -6) * mm, "end": v(-109.3, 43) * mm});
            skArc(sketch, "E74", {"start": v(-4.95, 22.32) * mm, "mid": v(-8.63, 21.17) * mm, "end": v(-12.07, 19.42) * mm});
            skArc(sketch, "E75.trimOffspring", {"start": v(22.32, 4.95) * mm, "mid": v(21.17, 8.63) * mm, "end": v(19.42, 12.07) * mm});
            skArc(sketch, "E76.trimOffspring", {"start": v(4.95, -22.32) * mm, "mid": v(8.63, -21.17) * mm, "end": v(12.07, -19.42) * mm});
            skArc(sketch, "E77.trimOffspring", {"start": v(-22.32, -4.95) * mm, "mid": v(-21.17, -8.63) * mm, "end": v(-19.42, -12.07) * mm});
            skSolve(sketch);
        }
        {
            var Q0;
            Q0=makeQuery(id+"F13.imprint","IMPRINT",FACE,{"disambiguationData":[TD([[makeQuery(id+"F13.imprint","IMPRINT",EDGE,{"derivedFrom":sQuery(id+"F13.wireOp",EDGE,"E66.0")}),-1.0]])]});
            var Q1;
            Q1=makeQuery(id+"F13.imprint","IMPRINT",FACE,{"disambiguationData":[TD([[makeQuery(id+"F13.imprint","IMPRINT",EDGE,{"derivedFrom":sQuery(id+"F13.wireOp",EDGE,"E45")}),1.0]])]});
            var Q2;
            Q2=makeQuery(id+"F13.imprint","IMPRINT",FACE,{"disambiguationData":[TD([[makeQuery(id+"F13.imprint","IMPRINT",EDGE,{"derivedFrom":sQuery(id+"F13.wireOp",EDGE,"E44")}),1.0]])]});
            var Q3;
            Q3=makeQuery(id+"F13.imprint","IMPRINT",FACE,{"disambiguationData":[TD([[makeQuery(id+"F13.imprint","IMPRINT",EDGE,{"derivedFrom":sQuery(id+"F13.wireOp",EDGE,"E47")}),1.0]])]});
            var Q4;
            Q4=makeQuery(id+"F13.imprint","IMPRINT",FACE,{"disambiguationData":[TD([[makeQuery(id+"F13.imprint","IMPRINT",EDGE,{"derivedFrom":sQuery(id+"F13.wireOp",EDGE,"E46")}),1.0]])]});
            var Q5;
            {var subQ1=sQuery(id+"F13.wireOp",EDGE,"E66.1");Q5=makeQuery(id+"F13.imprint","IMPRINT",FACE,{"disambiguationData":[TD([[makeQuery(id+"F13.imprint","IMPRINT",EDGE,{"derivedFrom":subQ1}),-1.0]])]});}
            extrude(context, id + "F14", {"entities" : qUnion([Q0, Q1, Q2, Q3, Q4, Q5]), "oppositeDirection" : true, "depth" : 30 * mm, "offsetDistance" : 25 * mm});
        }
        {
            var Q0;
            Q0=makeQuery(id+"F13.imprint","IMPRINT",FACE,{"disambiguationData":[TD([[makeQuery(id+"F13.imprint","IMPRINT",EDGE,{"derivedFrom":sQuery(id+"F13.wireOp",EDGE,"E43.bottom")}),1.0]])]});
            var Q1;
            {var subQ4=sQuery(id+"F13.wireOp",EDGE,"E66.0");Q1=makeQuery(id+"F13.imprint","IMPRINT",FACE,{"disambiguationData":[TD([[makeQuery(id+"F13.imprint","IMPRINT",EDGE,{"derivedFrom":subQ4}),1.0]])]});}
            extrude(context, id + "F15", {"entities" : qUnion([Q0, Q1]), "operationType" : NewBodyOperationType.ADD, "oppositeDirection" : true, "depth" : 29 * mm, "offsetDistance" : 25 * mm});
        }
        {
            var Q0;
            Q0=makeQuery(id+"F13.imprint","IMPRINT",FACE,{"disambiguationData":[TD([[makeQuery(id+"F13.imprint","IMPRINT",EDGE,{"derivedFrom":sQuery(id+"F13.wireOp",EDGE,"E54.1.0.0")}),1.0]])]});
            var Q1;
            Q1=makeQuery(id+"F13.imprint","IMPRINT",FACE,{"disambiguationData":[TD([[makeQuery(id+"F13.imprint","IMPRINT",EDGE,{"derivedFrom":sQuery(id+"F13.wireOp",EDGE,"E53")}),1.0]])]});
            extrude(context, id + "F16", {"entities" : qUnion([Q0, Q1]), "oppositeDirection" : true, "depth" : 7 * mm, "offsetDistance" : 25 * mm});
        }
        {
            var Q0;
            Q0=makeQuery(id+"F13.imprint","IMPRINT",FACE,{"disambiguationData":[TD([[makeQuery(id+"F13.imprint","IMPRINT",EDGE,{"derivedFrom":sQuery(id+"F13.wireOp",EDGE,"E43.bottom")}),1.0]])]});
            var Q1;
            Q1=makeQuery(id+"F13.imprint","IMPRINT",FACE,{"disambiguationData":[TD([[makeQuery(id+"F13.imprint","IMPRINT",EDGE,{"derivedFrom":sQuery(id+"F13.wireOp",EDGE,"E66.0")}),-1.0]])]});
            var Q2;
            Q2=makeQuery(id+"F13.imprint","IMPRINT",FACE,{"disambiguationData":[TD([[makeQuery(id+"F13.imprint","IMPRINT",EDGE,{"derivedFrom":sQuery(id+"F13.wireOp",EDGE,"E44")}),-1.0]])]});
            var Q3;
            Q3=makeQuery(id+"F13.imprint","IMPRINT",FACE,{"disambiguationData":[TD([[makeQuery(id+"F13.imprint","IMPRINT",EDGE,{"derivedFrom":sQuery(id+"F13.wireOp",EDGE,"E45")}),1.0]])]});
            var Q4;
            Q4=makeQuery(id+"F13.imprint","IMPRINT",FACE,{"disambiguationData":[TD([[makeQuery(id+"F13.imprint","IMPRINT",EDGE,{"derivedFrom":sQuery(id+"F13.wireOp",EDGE,"E44")}),1.0]])]});
            var Q5;
            Q5=makeQuery(id+"F13.imprint","IMPRINT",FACE,{"disambiguationData":[TD([[makeQuery(id+"F13.imprint","IMPRINT",EDGE,{"derivedFrom":sQuery(id+"F13.wireOp",EDGE,"E46")}),1.0]])]});
            var Q6;
            Q6=makeQuery(id+"F13.imprint","IMPRINT",FACE,{"disambiguationData":[TD([[makeQuery(id+"F13.imprint","IMPRINT",EDGE,{"derivedFrom":sQuery(id+"F13.wireOp",EDGE,"E47")}),1.0]])]});
            var Q7;
            Q7=makeQuery(id+"F13.imprint","IMPRINT",FACE,{"disambiguationData":[TD([[makeQuery(id+"F13.imprint","IMPRINT",EDGE,{"derivedFrom":sQuery(id+"F13.wireOp",EDGE,"E52.bottom")}),1.0]])]});
            var Q8;
            Q8=makeQuery(id+"F13.imprint","IMPRINT",FACE,{"disambiguationData":[TD([[makeQuery(id+"F13.imprint","IMPRINT",EDGE,{"derivedFrom":sQuery(id+"F13.wireOp",EDGE,"E54.1.0.0")}),1.0]])]});
            var Q9;
            Q9=makeQuery(id+"F13.imprint","IMPRINT",FACE,{"disambiguationData":[TD([[makeQuery(id+"F13.imprint","IMPRINT",EDGE,{"derivedFrom":sQuery(id+"F13.wireOp",EDGE,"E53")}),1.0]])]});
            var Q10;
            {var subQ0=sQuery(id+"F13.wireOp",EDGE,"E70");var subQ4=sQuery(id+"F13.wireOp",EDGE,"E43.top");var subQ5=makeQuery(id+"F13.imprint","INTERSECT",VERTEX,{"derivedFrom":[subQ4,subQ0]});Q10=makeQuery(id+"F13.imprint","IMPRINT",FACE,{"disambiguationData":[TD([[makeQuery(id+"F13.imprint","IMPRINT",EDGE,{"disambiguationData":[TD([[subQ5,-1.0]])],"derivedFrom":subQ4}),-1.0]])]});}
            var Q11;
            {var subQ0=sQuery(id+"F13.wireOp",EDGE,"E68");var subQ2=sQuery(id+"F13.wireOp",EDGE,"E43.left");var subQ3=makeQuery(id+"F13.imprint","INTERSECT",VERTEX,{"derivedFrom":[subQ2,subQ0]});Q11=makeQuery(id+"F13.imprint","IMPRINT",FACE,{"disambiguationData":[TD([[makeQuery(id+"F13.imprint","IMPRINT",EDGE,{"disambiguationData":[TD([[subQ3,-1.0]])],"derivedFrom":subQ2}),-1.0]])]});}
            var Q12;
            {var subQ1=sQuery(id+"F13.wireOp",EDGE,"E66.1");Q12=makeQuery(id+"F13.imprint","IMPRINT",FACE,{"disambiguationData":[TD([[makeQuery(id+"F13.imprint","IMPRINT",EDGE,{"derivedFrom":subQ1}),-1.0]])]});}
            var Q13;
            {var subQ4=sQuery(id+"F13.wireOp",EDGE,"E66.0");Q13=makeQuery(id+"F13.imprint","IMPRINT",FACE,{"disambiguationData":[TD([[makeQuery(id+"F13.imprint","IMPRINT",EDGE,{"derivedFrom":subQ4}),1.0]])]});}
            var Q14;
            Q14=makeQuery(id+"F13.imprint","IMPRINT",FACE,{"disambiguationData":[TD([[makeQuery(id+"F13.imprint","IMPRINT",EDGE,{"derivedFrom":sQuery(id+"F13.wireOp",EDGE,"E53")}),-1.0]])]});
            extrude(context, id + "F17", {"entities" : qUnion([Q0, Q1, Q2, Q3, Q4, Q5, Q6, Q7, Q8, Q9, Q10, Q11, Q12, Q13, Q14]), "depth" : 1.5 * mm, "offsetDistance" : 25 * mm});
        }
        {
            var Q0;
            {var subQ0=sQuery(id+"F13.wireOp",EDGE,"E62.trimOffspring");Q0=makeQuery(id+"F13.imprint","IMPRINT",FACE,{"disambiguationData":[TD([[makeQuery(id+"F13.imprint","IMPRINT",EDGE,{"derivedFrom":subQ0}),-1.0]])]});}
            var Q1;
            {var subQ0=sQuery(id+"F13.wireOp",EDGE,"E60");Q1=makeQuery(id+"F13.imprint","IMPRINT",FACE,{"disambiguationData":[TD([[makeQuery(id+"F13.imprint","IMPRINT",EDGE,{"derivedFrom":subQ0}),1.0]])]});}
            var Q2;
            {var subQ0=sQuery(id+"F13.wireOp",EDGE,"E58");Q2=makeQuery(id+"F13.imprint","IMPRINT",FACE,{"disambiguationData":[TD([[makeQuery(id+"F13.imprint","IMPRINT",EDGE,{"derivedFrom":subQ0}),1.0]])]});}
            var Q3;
            {var subQ0=sQuery(id+"F13.wireOp",EDGE,"E64.trimOffspring");Q3=makeQuery(id+"F13.imprint","IMPRINT",FACE,{"disambiguationData":[TD([[makeQuery(id+"F13.imprint","IMPRINT",EDGE,{"derivedFrom":subQ0}),-1.0]])]});}
            extrude(context, id + "F18", {"entities" : qUnion([Q0, Q1, Q2, Q3]), "depth" : 1 * mm, "offsetDistance" : 25 * mm});
        }
        {
            var Q0;
            Q0=sQuery(id+"F13.wireOp",VERTEX,"E54.direction1.start");
            var Q1;
            Q1=sQuery(id+"F13.wireOp",VERTEX,"E54.direction1.end");
            var Q2;
            Q2=makeQuery(id+"F16.opExtrude","SWEPT_BODY",BODY,{"disambiguationData":[OSD([sQuery(id+"F13.wireOp",EDGE,"E53")])]});
            var Q3;
            Q3=makeQuery(id+"F16.opExtrude","SWEPT_BODY",BODY,{"disambiguationData":[OSD([sQuery(id+"F13.wireOp",EDGE,"E54.1.0.0")])]});
            hole(context, id + "F19", {"style" : HoleStyle.SIMPLE, "endStyle" : HoleEndStyle.THROUGH, "holeDiameter" : 1.6 * mm, "majorDiameter" : 5 * mm, "isTappedThrough" : true, "tappedDepth" : 12 * mm, "tapClearance" : 3, "locations" : qUnion([Q0, Q1]), "scope" : qUnion([Q2, Q3])});
        }
        {
            var Q0;
            Q0=sQuery(id+"F13.wireOp",VERTEX,"E47.center");
            var Q1;
            Q1=sQuery(id+"F13.wireOp",VERTEX,"E46.center");
            var Q2;
            Q2=sQuery(id+"F13.wireOp",VERTEX,"E44.center");
            var Q3;
            Q3=sQuery(id+"F13.wireOp",VERTEX,"E45.center");
            var Q4;
            Q4=makeQuery(id+"F14.opExtrude","SWEPT_BODY",BODY,{"disambiguationData":[OSD([sQuery(id+"F13.wireOp",EDGE,"E44")])]});
            var Q5;
            Q5=makeQuery(id+"F14.opExtrude","SWEPT_BODY",BODY,{"disambiguationData":[OSD([sQuery(id+"F13.wireOp",EDGE,"E45")])]});
            var Q6;
            Q6=makeQuery(id+"F14.opExtrude","SWEPT_BODY",BODY,{"disambiguationData":[OSD([sQuery(id+"F13.wireOp",EDGE,"E46")])]});
            var Q7;
            Q7=makeQuery(id+"F14.opExtrude","SWEPT_BODY",BODY,{"disambiguationData":[OSD([sQuery(id+"F13.wireOp",EDGE,"E47")])]});
            hole(context, id + "F20", {"style" : HoleStyle.SIMPLE, "endStyle" : HoleEndStyle.THROUGH, "holeDiameter" : 1.6 * mm, "majorDiameter" : 5 * mm, "isTappedThrough" : true, "tappedDepth" : 12 * mm, "tapClearance" : 3, "locations" : qUnion([Q0, Q1, Q2, Q3]), "scope" : qUnion([Q4, Q5, Q6, Q7])});
        }
        {
            var Q0;
            Q0=makeQuery(id+"F18.opExtrude","SWEPT_BODY",BODY,{"disambiguationData":[OSD([sQuery(id+"F13.wireOp",EDGE,"E56"),sQuery(id+"F13.wireOp",EDGE,"E57"),sQuery(id+"F13.wireOp",EDGE,"E62.trimOffspring"),sQuery(id+"F13.wireOp",EDGE,"E63.trimOffspring")])]});
            var Q1;
            Q1=makeQuery(id+"F14.opExtrude","SWEPT_BODY",BODY,{"disambiguationData":[OSD([sQuery(id+"F13.wireOp",EDGE,"E44")])]});
            var Q2;
            Q2=makeQuery(id+"F14.opExtrude","SWEPT_BODY",BODY,{"disambiguationData":[OSD([sQuery(id+"F13.wireOp",EDGE,"E45")])]});
            var Q3;
            Q3=makeQuery(id+"F14.opExtrude","SWEPT_BODY",BODY,{"disambiguationData":[OSD([sQuery(id+"F13.wireOp",EDGE,"E46")])]});
            var Q4;
            Q4=makeQuery(id+"F14.opExtrude","SWEPT_BODY",BODY,{"disambiguationData":[OSD([sQuery(id+"F13.wireOp",EDGE,"E47")])]});
            var Q5;
            Q5=makeQuery(id+"F14.opExtrude","SWEPT_BODY",BODY,{"disambiguationData":[OSD([sQuery(id+"F13.wireOp",EDGE,"E66.0"),sQuery(id+"F13.wireOp",EDGE,"E66.1"),sQuery(id+"F13.wireOp",EDGE,"E66.2"),sQuery(id+"F13.wireOp",EDGE,"E66.3"),sQuery(id+"F13.wireOp",EDGE,"E67.0"),sQuery(id+"F13.wireOp",EDGE,"E67.1"),sQuery(id+"F13.wireOp",EDGE,"E67.2"),sQuery(id+"F13.wireOp",EDGE,"E67.3")])]});
            var Q6;
            Q6=makeQuery(id+"F16.opExtrude","SWEPT_BODY",BODY,{"disambiguationData":[OSD([sQuery(id+"F13.wireOp",EDGE,"E53")])]});
            var Q7;
            Q7=makeQuery(id+"F16.opExtrude","SWEPT_BODY",BODY,{"disambiguationData":[OSD([sQuery(id+"F13.wireOp",EDGE,"E54.1.0.0")])]});
            var Q8;
            Q8=makeQuery(id+"F17.opExtrude","SWEPT_BODY",BODY,{"disambiguationData":[OSD([sQuery(id+"F13.wireOp",EDGE,"E43.bottom"),sQuery(id+"F13.wireOp",EDGE,"E43.top"),sQuery(id+"F13.wireOp",EDGE,"E43.left"),sQuery(id+"F13.wireOp",EDGE,"E43.right"),sQuery(id+"F13.wireOp",EDGE,"E48"),sQuery(id+"F13.wireOp",EDGE,"E49.1.0.0"),sQuery(id+"F13.wireOp",EDGE,"E49.2.0.0"),sQuery(id+"F13.wireOp",EDGE,"E50"),sQuery(id+"F13.wireOp",EDGE,"E51.1.0.0"),sQuery(id+"F13.wireOp",EDGE,"E51.2.0.0"),sQuery(id+"F13.wireOp",EDGE,"E57")])]});
            var Q9;
            Q9=makeQuery(id+"F17.opExtrude","SWEPT_BODY",BODY,{"disambiguationData":[OSD([sQuery(id+"F13.wireOp",EDGE,"E52.bottom"),sQuery(id+"F13.wireOp",EDGE,"E52.top"),sQuery(id+"F13.wireOp",EDGE,"E52.left"),sQuery(id+"F13.wireOp",EDGE,"E52.right"),sQuery(id+"F13.wireOp",EDGE,"E56")])]});
            var Q10;
            Q10=makeQuery(id+"F18.opExtrude","SWEPT_BODY",BODY,{"disambiguationData":[OSD([sQuery(id+"F13.wireOp",EDGE,"E56"),sQuery(id+"F13.wireOp",EDGE,"E57"),sQuery(id+"F13.wireOp",EDGE,"E60"),sQuery(id+"F13.wireOp",EDGE,"E61")])]});
            var Q11;
            Q11=makeQuery(id+"F18.opExtrude","SWEPT_BODY",BODY,{"disambiguationData":[OSD([sQuery(id+"F13.wireOp",EDGE,"E56"),sQuery(id+"F13.wireOp",EDGE,"E57"),sQuery(id+"F13.wireOp",EDGE,"E58"),sQuery(id+"F13.wireOp",EDGE,"E59")])]});
            var Q12;
            Q12=makeQuery(id+"F18.opExtrude","SWEPT_BODY",BODY,{"disambiguationData":[OSD([sQuery(id+"F13.wireOp",EDGE,"E56"),sQuery(id+"F13.wireOp",EDGE,"E57"),sQuery(id+"F13.wireOp",EDGE,"E64.trimOffspring"),sQuery(id+"F13.wireOp",EDGE,"E65.trimOffspring")])]});
            var Q13;
            Q13=makeQuery(id+"F15.opExtrude","SWEPT_BODY",BODY,{"disambiguationData":[OSD([sQuery(id+"F13.wireOp",EDGE,"E43.top"),sQuery(id+"F13.wireOp",EDGE,"E43.left"),sQuery(id+"F13.wireOp",EDGE,"E66.0"),sQuery(id+"F13.wireOp",EDGE,"E69"),sQuery(id+"F13.wireOp",EDGE,"E70"),sQuery(id+"F13.wireOp",EDGE,"E73.trimOffspring")])]});
            var Q14;
            Q14=makeQuery(id+"F14.opExtrude","SWEPT_BODY",BODY,{"disambiguationData":[OSD([sQuery(id+"F13.wireOp",EDGE,"E66.0"),sQuery(id+"F13.wireOp",EDGE,"E67.0"),sQuery(id+"F13.wireOp",EDGE,"E67.1"),sQuery(id+"F13.wireOp",EDGE,"E69"),sQuery(id+"F13.wireOp",EDGE,"E70"),sQuery(id+"F13.wireOp",EDGE,"E73.trimOffspring")])]});
            booleanBodies(context, id + "F21", {"operationType" : BooleanOperationType.UNION, "tools" : qUnion([Q0, Q1, Q2, Q3, Q4, Q5, Q6, Q7, Q8, Q9, Q10, Q11, Q12, Q13, Q14])});
        }
        {
            var Q0;
            Q0=makeQuery(id+"F14.opExtrude","SWEPT_EDGE",EDGE,{"disambiguationData":[OSD([sQuery(id+"F13.wireOp",EDGE,"E66.0"),sQuery(id+"F13.wireOp",EDGE,"E73.trimOffspring")])]});
            var Q1;
            Q1=makeQuery(id+"F14.opExtrude","SWEPT_EDGE",EDGE,{"disambiguationData":[OSD([sQuery(id+"F13.wireOp",EDGE,"E66.1"),sQuery(id+"F13.wireOp",EDGE,"E66.2")])]});
            var Q2;
            Q2=makeQuery(id+"F14.opExtrude","SWEPT_EDGE",EDGE,{"disambiguationData":[OSD([sQuery(id+"F13.wireOp",EDGE,"E66.2"),sQuery(id+"F13.wireOp",EDGE,"E66.3")])]});
            var Q3;
            Q3=makeQuery(id+"F14.opExtrude","SWEPT_EDGE",EDGE,{"disambiguationData":[OSD([sQuery(id+"F13.wireOp",EDGE,"E66.3"),sQuery(id+"F13.wireOp",EDGE,"E72.trimOffspring")])]});
            var Q4;
            Q4=makeQuery(id+"F14.opExtrude","SWEPT_EDGE",EDGE,{"disambiguationData":[OSD([sQuery(id+"F13.wireOp",EDGE,"E67.2"),sQuery(id+"F13.wireOp",EDGE,"E67.3")])]});
            var Q5;
            Q5=makeQuery(id+"F14.opExtrude","SWEPT_EDGE",EDGE,{"disambiguationData":[OSD([sQuery(id+"F13.wireOp",EDGE,"E67.0"),sQuery(id+"F13.wireOp",EDGE,"E67.3")])]});
            var Q6;
            Q6=makeQuery(id+"F14.opExtrude","SWEPT_EDGE",EDGE,{"disambiguationData":[OSD([sQuery(id+"F13.wireOp",EDGE,"E67.0"),sQuery(id+"F13.wireOp",EDGE,"E67.1")])]});
            var Q7;
            Q7=makeQuery(id+"F14.opExtrude","SWEPT_EDGE",EDGE,{"disambiguationData":[OSD([sQuery(id+"F13.wireOp",EDGE,"E67.1"),sQuery(id+"F13.wireOp",EDGE,"E67.2")])]});
            var Q8;
            {var subQ0=sQuery(id+"F13.wireOp",EDGE,"E43.left");var subQ1=sQuery(id+"F13.wireOp",EDGE,"E43.bottom");Q8=makeQuery(id+"F21.opBoolean","MERGE",EDGE,{"derivedFrom":[makeQuery(id+"F15.opExtrude","SWEPT_EDGE",EDGE,{"disambiguationData":[OSD([subQ1,subQ0])]}),makeQuery(id+"F17.opExtrude","SWEPT_EDGE",EDGE,{"disambiguationData":[OSD([subQ1,subQ0])]})]});}
            var Q9;
            {var subQ0=sQuery(id+"F13.wireOp",EDGE,"E43.right");var subQ1=sQuery(id+"F13.wireOp",EDGE,"E43.top");Q9=makeQuery(id+"F21.opBoolean","MERGE",EDGE,{"derivedFrom":[makeQuery(id+"F15.opExtrude","SWEPT_EDGE",EDGE,{"disambiguationData":[OSD([subQ1,subQ0])]}),makeQuery(id+"F17.opExtrude","SWEPT_EDGE",EDGE,{"disambiguationData":[OSD([subQ1,subQ0])]})]});}
            var Q10;
            {var subQ0=sQuery(id+"F13.wireOp",EDGE,"E43.right");var subQ1=sQuery(id+"F13.wireOp",EDGE,"E43.bottom");Q10=makeQuery(id+"F21.opBoolean","MERGE",EDGE,{"derivedFrom":[makeQuery(id+"F15.opExtrude","SWEPT_EDGE",EDGE,{"disambiguationData":[OSD([subQ1,subQ0])]}),makeQuery(id+"F17.opExtrude","SWEPT_EDGE",EDGE,{"disambiguationData":[OSD([subQ1,subQ0])]})]});}
            var Q11;
            {var subQ0=sQuery(id+"F13.wireOp",EDGE,"E43.left");var subQ1=sQuery(id+"F13.wireOp",EDGE,"E43.top");Q11=makeQuery(id+"F21.opBoolean","MERGE",EDGE,{"derivedFrom":[makeQuery(id+"F15.opExtrude","SWEPT_EDGE",EDGE,{"disambiguationData":[OSD([subQ1,subQ0])]}),makeQuery(id+"F17.opExtrude","SWEPT_EDGE",EDGE,{"disambiguationData":[OSD([subQ1,subQ0])]})]});}
            fillet(context, id + "F22", {"entities" : qUnion([Q0, Q1, Q2, Q3, Q4, Q5, Q6, Q7, Q8, Q9, Q10, Q11]), "radius" : 2 * mm, "tangentPropagation" : true, "allowEdgeOverflow" : false});
        }
        {
            var Q0;
            {var subQ0=sQuery(id+"F13.wireOp",EDGE,"E70");var subQ4=sQuery(id+"F13.wireOp",EDGE,"E43.top");var subQ5=makeQuery(id+"F13.imprint","INTERSECT",VERTEX,{"derivedFrom":[subQ4,subQ0]});Q0=makeQuery(id+"F13.imprint","IMPRINT",FACE,{"disambiguationData":[TD([[makeQuery(id+"F13.imprint","IMPRINT",EDGE,{"disambiguationData":[TD([[subQ5,-1.0]])],"derivedFrom":subQ4}),-1.0]])]});}
            extrude(context, id + "F23", {"entities" : qUnion([Q0]), "operationType" : NewBodyOperationType.ADD, "oppositeDirection" : true, "depth" : 28 * mm, "offsetDistance" : 25 * mm});
        }
        {
            var Q0;
            {var subQ0=sQuery(id+"F13.wireOp",EDGE,"E68");var subQ2=sQuery(id+"F13.wireOp",EDGE,"E43.left");var subQ3=makeQuery(id+"F13.imprint","INTERSECT",VERTEX,{"derivedFrom":[subQ2,subQ0]});Q0=makeQuery(id+"F13.imprint","IMPRINT",FACE,{"disambiguationData":[TD([[makeQuery(id+"F13.imprint","IMPRINT",EDGE,{"disambiguationData":[TD([[subQ3,-1.0]])],"derivedFrom":subQ2}),-1.0]])]});}
            extrude(context, id + "F24", {"entities" : qUnion([Q0]), "operationType" : NewBodyOperationType.ADD, "oppositeDirection" : true, "depth" : 27 * mm, "offsetDistance" : 25 * mm});
        }
        {
            var Q0;
            Q0=qCreatedBy(makeId("Right.planeOp"),FACE);
            cPlane(context, id + "F25", {"entities" : qUnion([Q0]), "cplaneType" : CPlaneType.OFFSET, "offset" : 40.2 * mm, "width" : 150 * mm, "height" : 150 * mm});
        }
        {
            var Q0;
            Q0=qCreatedBy(id+"F25.planeOp",FACE);
            var sketch = newSketch(context, id + "F26", { "sketchPlane" : qUnion([Q0])});
            skCircle(sketch, "E78", {"center": v(-2.5, 8.85) * mm, "radius": 0.75 * mm});
            skCircle(sketch, "E79.1.0.0", {"center": v(0, 8.85) * mm, "radius": 0.75 * mm});
            skCircle(sketch, "E79.2.0.0", {"center": v(2.5, 8.85) * mm, "radius": 0.75 * mm});
            skLineSegment(sketch, "E79.direction1", {"start": v(-2.5, 8.85) * mm, "end": v(0, 8.85) * mm, "construction": true});
            skCircle(sketch, "E80.1.0.0", {"center": v(-2.5, 6.35) * mm, "radius": 0.75 * mm});
            skCircle(sketch, "E80.1.0.1", {"center": v(0, 6.35) * mm, "radius": 0.75 * mm});
            skCircle(sketch, "E80.1.0.2", {"center": v(2.5, 6.35) * mm, "radius": 0.75 * mm});
            skLineSegment(sketch, "E80.direction1", {"start": v(-2.5, 8.85) * mm, "end": v(-2.5, 6.35) * mm, "construction": true});
            skCircle(sketch, "E81.1.0.0", {"center": v(-2.5, 72.35) * mm, "radius": 0.75 * mm});
            skCircle(sketch, "E81.1.0.1", {"center": v(0, 72.35) * mm, "radius": 0.75 * mm});
            skCircle(sketch, "E81.1.0.2", {"center": v(2.5, 72.35) * mm, "radius": 0.75 * mm});
            skLineSegment(sketch, "E81.direction1", {"start": v(-2.5, 8.85) * mm, "end": v(-2.5, 72.35) * mm, "construction": true});
            skSolve(sketch);
        }
        {
            var Q0;
            Q0 = qSketchRegion(id + "F26", true);
            extrude(context, id + "F27", {"entities" : qUnion([Q0]), "oppositeDirection" : true, "depth" : 1.5 * mm, "offsetDistance" : 25 * mm});
        }
        {
            var Q0;
            Q0=makeQuery(id+"F27.opExtrude","SWEPT_BODY",BODY,{"disambiguationData":[OSD([sQuery(id+"F26.wireOp",EDGE,"E78")])]});
            var Q1;
            Q1=makeQuery(id+"F27.opExtrude","SWEPT_BODY",BODY,{"disambiguationData":[OSD([sQuery(id+"F26.wireOp",EDGE,"E80.1.0.0")])]});
            var Q2;
            Q2=makeQuery(id+"F27.opExtrude","SWEPT_BODY",BODY,{"disambiguationData":[OSD([sQuery(id+"F26.wireOp",EDGE,"E80.1.0.1")])]});
            var Q3;
            Q3=makeQuery(id+"F27.opExtrude","SWEPT_BODY",BODY,{"disambiguationData":[OSD([sQuery(id+"F26.wireOp",EDGE,"E80.1.0.2")])]});
            var Q4;
            Q4=makeQuery(id+"F27.opExtrude","SWEPT_BODY",BODY,{"disambiguationData":[OSD([sQuery(id+"F26.wireOp",EDGE,"E79.1.0.0")])]});
            var Q5;
            Q5=makeQuery(id+"F27.opExtrude","SWEPT_BODY",BODY,{"disambiguationData":[OSD([sQuery(id+"F26.wireOp",EDGE,"E79.2.0.0")])]});
            var Q6;
            Q6=makeQuery(id+"F1.opExtrude","SWEPT_BODY",BODY,{"disambiguationData":[OSD([sQuery(id+"F0.wireOp",EDGE,"E0"),sQuery(id+"F0.wireOp",EDGE,"E7.bottom"),sQuery(id+"F0.wireOp",EDGE,"E8"),sQuery(id+"F0.wireOp",EDGE,"E12.trimOffspring")])]});
            booleanBodies(context, id + "F28", {"operationType" : BooleanOperationType.SUBTRACTION, "tools" : qUnion([Q0, Q1, Q2, Q3, Q4, Q5]), "targets" : qUnion([Q6])});
        }
        {
            var Q0;
            Q0=makeQuery(id+"F27.opExtrude","SWEPT_BODY",BODY,{"disambiguationData":[OSD([sQuery(id+"F26.wireOp",EDGE,"E81.1.0.0")])]});
            var Q1;
            Q1=makeQuery(id+"F27.opExtrude","SWEPT_BODY",BODY,{"disambiguationData":[OSD([sQuery(id+"F26.wireOp",EDGE,"E81.1.0.1")])]});
            var Q2;
            Q2=makeQuery(id+"F27.opExtrude","SWEPT_BODY",BODY,{"disambiguationData":[OSD([sQuery(id+"F26.wireOp",EDGE,"E81.1.0.2")])]});
            var Q3;
            Q3=makeQuery(id+"F18.opExtrude","SWEPT_BODY",BODY,{"disambiguationData":[OSD([sQuery(id+"F13.wireOp",EDGE,"E56"),sQuery(id+"F13.wireOp",EDGE,"E57"),sQuery(id+"F13.wireOp",EDGE,"E58"),sQuery(id+"F13.wireOp",EDGE,"E59"),sQuery(id+"F13.wireOp",EDGE,"E60"),sQuery(id+"F13.wireOp",EDGE,"E61"),sQuery(id+"F13.wireOp",EDGE,"E62.trimOffspring"),sQuery(id+"F13.wireOp",EDGE,"E63.trimOffspring"),sQuery(id+"F13.wireOp",EDGE,"E64.trimOffspring"),sQuery(id+"F13.wireOp",EDGE,"E65.trimOffspring"),sQuery(id+"F13.wireOp",EDGE,"E74"),sQuery(id+"F13.wireOp",EDGE,"E75.trimOffspring"),sQuery(id+"F13.wireOp",EDGE,"E76.trimOffspring"),sQuery(id+"F13.wireOp",EDGE,"E77.trimOffspring")])]});
            booleanBodies(context, id + "F29", {"operationType" : BooleanOperationType.SUBTRACTION, "tools" : qUnion([Q0, Q1, Q2]), "targets" : qUnion([Q3])});
        }
    });
